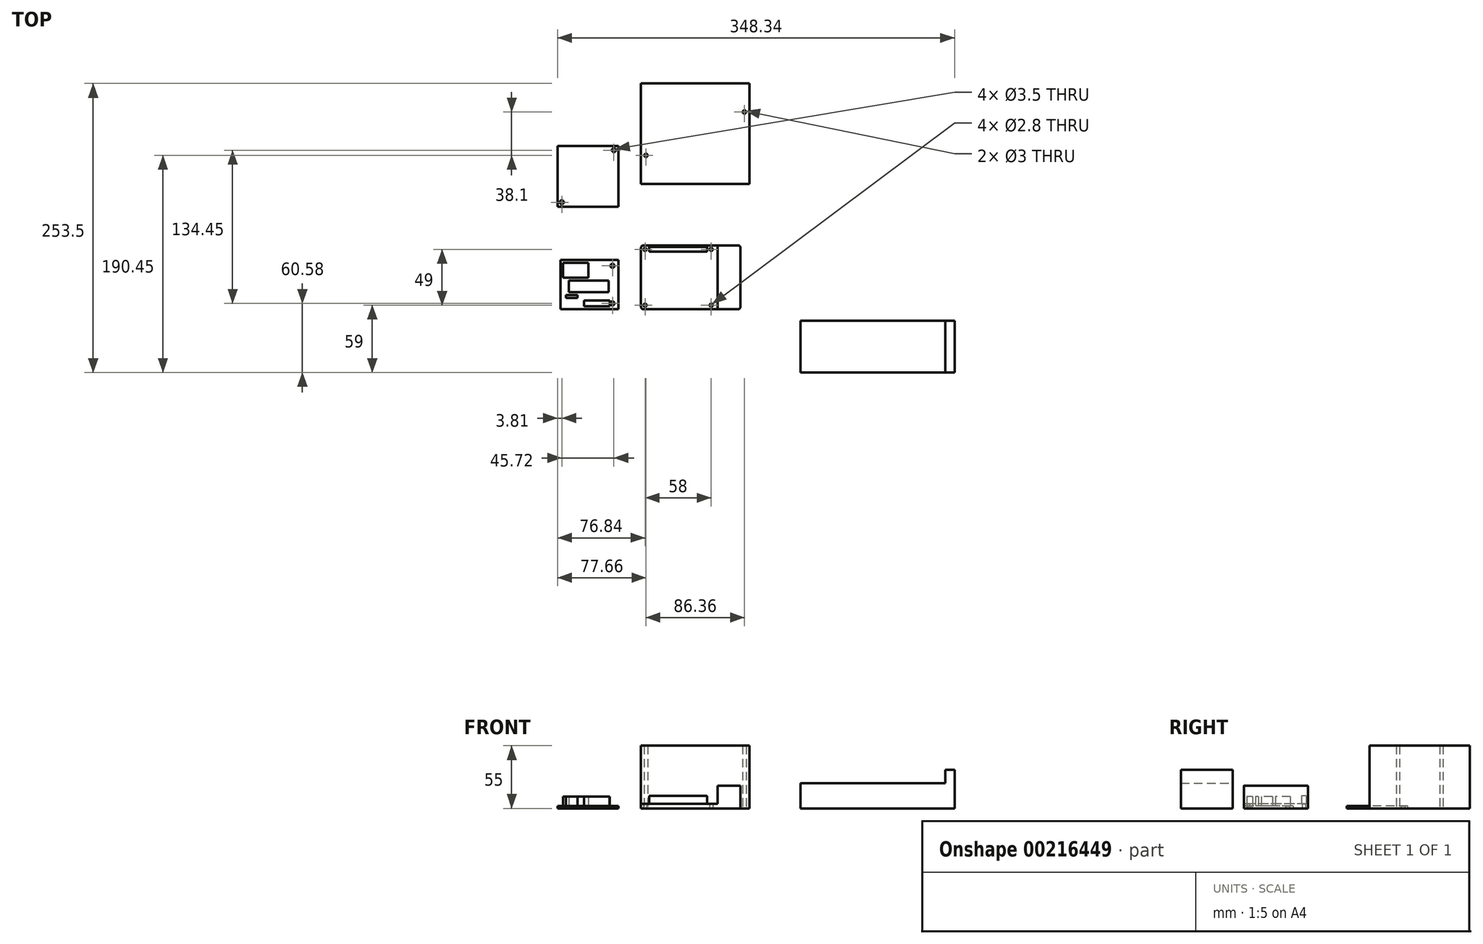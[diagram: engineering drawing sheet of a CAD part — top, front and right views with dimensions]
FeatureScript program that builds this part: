
annotation { "Feature Type Name" : "Feature", "Feature Type Description" : "" }
export const myFeature = defineFeature(function(context is Context, id is Id, definition is map)
    precondition{}
    {
        {
            var Q0;
            Q0=qCreatedBy(makeId("Top.planeOp"),FACE);
            var sketch = newSketch(context, id + "F0", { "sketchPlane" : qUnion([Q0])});
            skLineSegment(sketch, "E0.bottom", {"start": v(12, 66) * mm, "end": v(95.1, 66) * mm});
            skLineSegment(sketch, "E0.top", {"start": v(12, 10) * mm, "end": v(95.1, 10) * mm});
            skLineSegment(sketch, "E0.left", {"start": v(10, 64) * mm, "end": v(10, 12) * mm});
            skLineSegment(sketch, "E0.right", {"start": v(97.1, 64) * mm, "end": v(97.1, 12) * mm});
            skCircle(sketch, "E1", {"center": v(13.5, 62.5) * mm, "radius": 1.4 * mm});
            skCircle(sketch, "E2", {"center": v(71.5, 62.5) * mm, "radius": 1.4 * mm});
            skCircle(sketch, "E3", {"center": v(71.5, 13.5) * mm, "radius": 1.4 * mm});
            skCircle(sketch, "E4", {"center": v(13.5, 13.5) * mm, "radius": 1.4 * mm});
            skPoint(sketch, "E5.visualSharp", {"position": v(10, 10) * mm});
            skArc(sketch, "E5.filletArc", {"start": v(10, 12) * mm, "mid": v(10.59, 10.59) * mm, "end": v(12, 10) * mm});
            skPoint(sketch, "E6.visualSharp", {"position": v(10, 66) * mm});
            skArc(sketch, "E6.filletArc", {"start": v(12, 66) * mm, "mid": v(10.59, 65.41) * mm, "end": v(10, 64) * mm});
            skPoint(sketch, "E7.visualSharp", {"position": v(97.1, 66) * mm});
            skArc(sketch, "E7.filletArc", {"start": v(97.1, 64) * mm, "mid": v(96.51, 65.41) * mm, "end": v(95.1, 66) * mm});
            skPoint(sketch, "E8.visualSharp", {"position": v(97.1, 10) * mm});
            skArc(sketch, "E8.filletArc", {"start": v(95.1, 10) * mm, "mid": v(96.51, 10.59) * mm, "end": v(97.1, 12) * mm});
            skSolve(sketch);
        }
        {
            var Q0;
            Q0 = qSketchRegion(id + "F0", true);
            extrude(context, id + "F1", {"entities" : qUnion([Q0]), "depth" : 4 * mm});
        }
        {
            var Q0;
            Q0=makeQuery(id+"F1.opExtrude","CAP_FACE",FACE,{"disambiguationData":[OSD([sQuery(id+"F0.wireOp",EDGE,"E0.bottom"),sQuery(id+"F0.wireOp",EDGE,"E0.top"),sQuery(id+"F0.wireOp",EDGE,"E0.left"),sQuery(id+"F0.wireOp",EDGE,"E0.right"),sQuery(id+"F0.wireOp",EDGE,"E1"),sQuery(id+"F0.wireOp",EDGE,"E2"),sQuery(id+"F0.wireOp",EDGE,"E3"),sQuery(id+"F0.wireOp",EDGE,"E4")])],"isStart":false});
            var sketch = newSketch(context, id + "F2", { "sketchPlane" : qUnion([Q0])});
            skLineSegment(sketch, "E9", {"start": v(13.5, 62.5) * mm, "end": v(71.5, 62.5) * mm, "construction": true});
            skLineSegment(sketch, "E10.bottom", {"start": v(17.1, 64.5) * mm, "end": v(67.9, 64.5) * mm});
            skLineSegment(sketch, "E10.top", {"start": v(17.1, 60.5) * mm, "end": v(67.9, 60.5) * mm});
            skLineSegment(sketch, "E10.left", {"start": v(17.1, 64.5) * mm, "end": v(17.1, 60.5) * mm});
            skLineSegment(sketch, "E10.right", {"start": v(67.9, 64.5) * mm, "end": v(67.9, 60.5) * mm});
            skPoint(sketch, "E11", {"position": v(17.1, 62.5) * mm});
            skPoint(sketch, "E12", {"position": v(42.5, 62.5) * mm});
            skPoint(sketch, "E13", {"position": v(42.5, 64.5) * mm});
            skLineSegment(sketch, "E14.bottom", {"start": v(97.1, 66) * mm, "end": v(77.1, 66) * mm, "construction": true});
            skLineSegment(sketch, "E14.top", {"start": v(97.1, 10) * mm, "end": v(77.1, 10) * mm, "construction": true});
            skLineSegment(sketch, "E14.left", {"start": v(97.1, 66) * mm, "end": v(97.1, 10) * mm, "construction": true});
            skLineSegment(sketch, "E14.right", {"start": v(77.1, 66) * mm, "end": v(77.1, 10) * mm, "construction": true});
            skSolve(sketch);
        }
        {
            var Q0;
            Q0 = qSketchRegion(id + "F2", true);
            extrude(context, id + "F3", {"entities" : qUnion([Q0]), "operationType" : NewBodyOperationType.ADD, "depth" : 7 * mm});
        }
        {
            var Q0;
            Q0=makeQuery(id+"F1.opExtrude","CAP_FACE",FACE,{"disambiguationData":[OSD([sQuery(id+"F0.wireOp",EDGE,"E0.bottom"),sQuery(id+"F0.wireOp",EDGE,"E0.top"),sQuery(id+"F0.wireOp",EDGE,"E0.left"),sQuery(id+"F0.wireOp",EDGE,"E0.right"),sQuery(id+"F0.wireOp",EDGE,"E1"),sQuery(id+"F0.wireOp",EDGE,"E2"),sQuery(id+"F0.wireOp",EDGE,"E3"),sQuery(id+"F0.wireOp",EDGE,"E4")])],"isStart":false});
            var sketch = newSketch(context, id + "F4", { "sketchPlane" : qUnion([Q0])});
            skLineSegment(sketch, "E15.bottom", {"start": v(95.1, 66) * mm, "end": v(77.1, 66) * mm});
            skLineSegment(sketch, "E15.top", {"start": v(95.1, 10) * mm, "end": v(77.1, 10) * mm});
            skLineSegment(sketch, "E15.left", {"start": v(97.1, 64) * mm, "end": v(97.1, 12) * mm});
            skLineSegment(sketch, "E15.right", {"start": v(77.1, 66) * mm, "end": v(77.1, 10) * mm});
            skPoint(sketch, "E16.visualSharp", {"position": v(97.1, 66) * mm});
            skArc(sketch, "E16.filletArc", {"start": v(97.1, 64) * mm, "mid": v(96.51, 65.41) * mm, "end": v(95.1, 66) * mm});
            skPoint(sketch, "E17.visualSharp", {"position": v(97.1, 10) * mm});
            skArc(sketch, "E17.filletArc", {"start": v(95.1, 10) * mm, "mid": v(96.51, 10.59) * mm, "end": v(97.1, 12) * mm});
            skSolve(sketch);
        }
        {
            var Q0;
            Q0 = qSketchRegion(id + "F4", true);
            extrude(context, id + "F5", {"entities" : qUnion([Q0]), "operationType" : NewBodyOperationType.ADD, "depth" : 16 * mm});
        }
        {
            var Q0;
            Q0=qCreatedBy(makeId("Top.planeOp"),FACE);
            var sketch = newSketch(context, id + "F6", { "sketchPlane" : qUnion([Q0])});
            skLineSegment(sketch, "E18.bottom", {"start": v(10, 120) * mm, "end": v(105, 120) * mm});
            skLineSegment(sketch, "E18.top", {"start": v(10, 208) * mm, "end": v(105, 208) * mm});
            skLineSegment(sketch, "E18.left", {"start": v(10, 120) * mm, "end": v(10, 208) * mm});
            skLineSegment(sketch, "E18.right", {"start": v(105, 120) * mm, "end": v(105, 208) * mm});
            skLineSegment(sketch, "E19", {"start": v(10, 164) * mm, "end": v(105, 164) * mm, "construction": true});
            skLineSegment(sketch, "E20", {"start": v(57.5, 164) * mm, "end": v(54.56, 170.67) * mm, "construction": true});
            skLineSegment(sketch, "E21", {"start": v(57.5, 164) * mm, "end": v(100.68, 183.05) * mm, "construction": true});
            skCircle(sketch, "E22", {"center": v(100.68, 183.05) * mm, "radius": 1.5 * mm});
            skCircle(sketch, "E23.MirrorC", {"center": v(14.32, 144.95) * mm, "radius": 1.5 * mm});
            skSolve(sketch);
        }
        {
            var Q0;
            Q0 = qSketchRegion(id + "F6", true);
            extrude(context, id + "F7", {"entities" : qUnion([Q0]), "depth" : 55 * mm});
        }
        {
            var Q0;
            Q0=qCreatedBy(makeId("Top.planeOp"),FACE);
            var sketch = newSketch(context, id + "F8", { "sketchPlane" : qUnion([Q0])});
            skLineSegment(sketch, "E24.bottom", {"start": v(-60.8, 53.18) * mm, "end": v(-10, 53.18) * mm});
            skLineSegment(sketch, "E24.top", {"start": v(-60.8, 10) * mm, "end": v(-10, 10) * mm});
            skLineSegment(sketch, "E24.left", {"start": v(-60.8, 53.18) * mm, "end": v(-60.8, 10) * mm});
            skLineSegment(sketch, "E24.right", {"start": v(-10, 53.18) * mm, "end": v(-10, 10) * mm});
            skLineSegment(sketch, "E25.bottom", {"start": v(-63.34, 153.34) * mm, "end": v(-10, 153.34) * mm});
            skLineSegment(sketch, "E25.top", {"start": v(-63.34, 100) * mm, "end": v(-10, 100) * mm});
            skLineSegment(sketch, "E25.left", {"start": v(-63.34, 153.34) * mm, "end": v(-63.34, 100) * mm});
            skLineSegment(sketch, "E25.right", {"start": v(-10, 153.34) * mm, "end": v(-10, 100) * mm});
            skCircle(sketch, "E26", {"center": v(-15.08, 15.08) * mm, "radius": 1.75 * mm});
            skLineSegment(sketch, "E27", {"start": v(-10, 31.59) * mm, "end": v(-19.87, 31.59) * mm, "construction": true});
            skCircle(sketch, "E28.MirrorC", {"center": v(-15.08, 48.1) * mm, "radius": 1.75 * mm});
            skLineSegment(sketch, "E29", {"start": v(-15.08, 48.1) * mm, "end": v(-15.08, 53.18) * mm, "construction": true});
            skLineSegment(sketch, "E30", {"start": v(-15.08, 48.1) * mm, "end": v(-10, 48.1) * mm, "construction": true});
            skLineSegment(sketch, "E31", {"start": v(-36.67, 153.34) * mm, "end": v(-36.67, 126.67) * mm, "construction": true});
            skLineSegment(sketch, "E32", {"start": v(-36.67, 126.67) * mm, "end": v(-10, 126.67) * mm, "construction": true});
            skLineSegment(sketch, "E33", {"start": v(-17.62, 153.34) * mm, "end": v(-10, 145.72) * mm, "construction": true});
            skCircle(sketch, "E34", {"center": v(-13.81, 149.53) * mm, "radius": 1.75 * mm});
            skCircle(sketch, "E35.MirrorC", {"center": v(-13.81, 103.81) * mm, "radius": 1.75 * mm, "construction": true});
            skCircle(sketch, "E36.MirrorC", {"center": v(-59.53, 103.81) * mm, "radius": 1.75 * mm});
            skSolve(sketch);
        }
        {
            var Q0;
            Q0 = qSketchRegion(id + "F8", true);
            extrude(context, id + "F9", {"entities" : qUnion([Q0]), "depth" : 2 * mm});
        }
        {
            var Q0;
            Q0=makeQuery(id+"F9.opExtrude","CAP_FACE",FACE,{"disambiguationData":[OSD([sQuery(id+"F8.wireOp",EDGE,"E24.bottom"),sQuery(id+"F8.wireOp",EDGE,"E24.top"),sQuery(id+"F8.wireOp",EDGE,"E24.left"),sQuery(id+"F8.wireOp",EDGE,"E24.right")])],"isStart":false});
            var sketch = newSketch(context, id + "F10", { "sketchPlane" : qUnion([Q0])});
            skLineSegment(sketch, "E37.bottom", {"start": v(-53.3, 35) * mm, "end": v(-18.3, 35) * mm});
            skLineSegment(sketch, "E37.top", {"start": v(-53.3, 25) * mm, "end": v(-18.3, 25) * mm});
            skLineSegment(sketch, "E37.left", {"start": v(-53.3, 35) * mm, "end": v(-53.3, 25) * mm});
            skLineSegment(sketch, "E37.right", {"start": v(-18.3, 35) * mm, "end": v(-18.3, 25) * mm});
            skLineSegment(sketch, "E38.bottom", {"start": v(-40, 17.5) * mm, "end": v(-17.5, 17.5) * mm});
            skLineSegment(sketch, "E38.top", {"start": v(-40, 12.5) * mm, "end": v(-17.5, 12.5) * mm});
            skLineSegment(sketch, "E38.left", {"start": v(-40, 17.5) * mm, "end": v(-40, 12.5) * mm});
            skLineSegment(sketch, "E38.right", {"start": v(-17.5, 17.5) * mm, "end": v(-17.5, 12.5) * mm});
            skLineSegment(sketch, "E39.bottom", {"start": v(-55.8, 22.5) * mm, "end": v(-45.8, 22.5) * mm});
            skLineSegment(sketch, "E39.top", {"start": v(-55.8, 20) * mm, "end": v(-45.8, 20) * mm});
            skLineSegment(sketch, "E39.left", {"start": v(-55.8, 22.5) * mm, "end": v(-55.8, 20) * mm});
            skLineSegment(sketch, "E39.right", {"start": v(-45.8, 22.5) * mm, "end": v(-45.8, 20) * mm});
            skLineSegment(sketch, "E40.bottom", {"start": v(-58.3, 50.68) * mm, "end": v(-36.3, 50.68) * mm});
            skLineSegment(sketch, "E40.top", {"start": v(-58.3, 37.5) * mm, "end": v(-36.3, 37.5) * mm});
            skLineSegment(sketch, "E40.left", {"start": v(-58.3, 50.68) * mm, "end": v(-58.3, 37.5) * mm});
            skLineSegment(sketch, "E40.right", {"start": v(-36.3, 50.68) * mm, "end": v(-36.3, 37.5) * mm});
            skSolve(sketch);
        }
        {
            var Q0;
            Q0 = qSketchRegion(id + "F10", true);
            extrude(context, id + "F11", {"entities" : qUnion([Q0]), "operationType" : NewBodyOperationType.ADD, "depth" : 8.3 * mm});
        }
        {
            var Q0;
            Q0=qCreatedBy(makeId("Front.planeOp"),FACE);
            var sketch = newSketch(context, id + "F12", { "sketchPlane" : qUnion([Q0])});
            skLineSegment(sketch, "E41.bottom", {"start": v(150, 0) * mm, "end": v(285, 0) * mm});
            skLineSegment(sketch, "E41.top", {"start": v(150, 22) * mm, "end": v(277, 22) * mm});
            skLineSegment(sketch, "E41.left", {"start": v(150, 0) * mm, "end": v(150, 22) * mm});
            skLineSegment(sketch, "E41.right", {"start": v(285, 0) * mm, "end": v(285, 22) * mm});
            skLineSegment(sketch, "E42", {"start": v(285, 22) * mm, "end": v(285, 34) * mm});
            skLineSegment(sketch, "E43", {"start": v(285, 34) * mm, "end": v(277, 34) * mm});
            skLineSegment(sketch, "E44", {"start": v(277, 34) * mm, "end": v(277, 22) * mm});
            skLineSegment(sketch, "E45", {"start": v(277, 22) * mm, "end": v(285, 22) * mm, "construction": true});
            skSolve(sketch);
        }
        {
            var Q0;
            Q0 = qSketchRegion(id + "F12", true);
            extrude(context, id + "F13", {"entities" : qUnion([Q0]), "depth" : 45.5 * mm});
        }
    });
